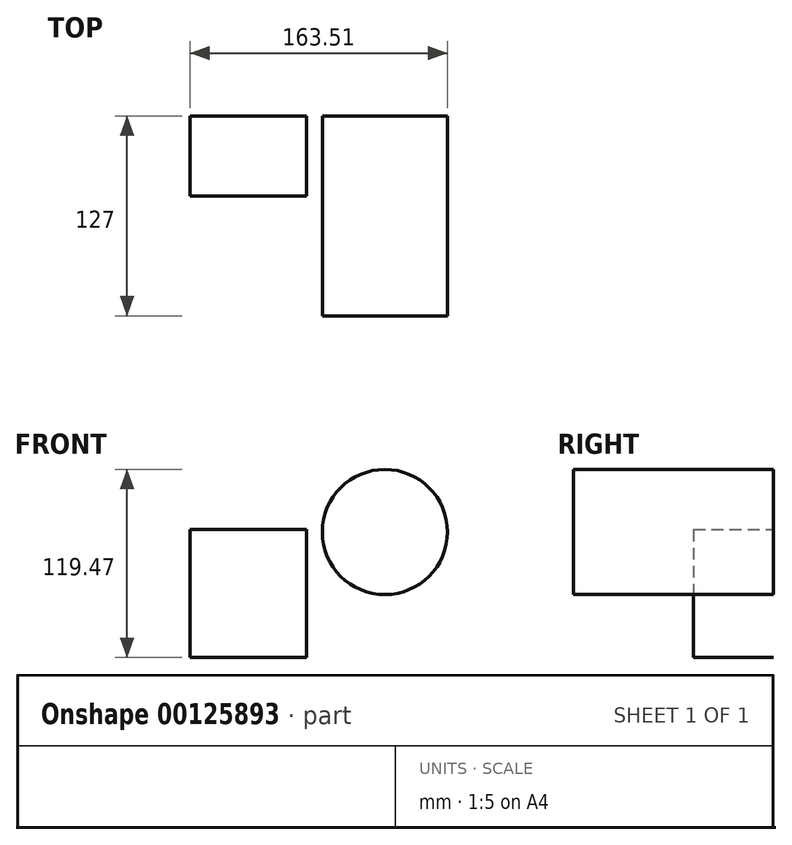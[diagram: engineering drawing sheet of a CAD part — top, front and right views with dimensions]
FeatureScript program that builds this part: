
annotation { "Feature Type Name" : "Feature", "Feature Type Description" : "" }
export const myFeature = defineFeature(function(context is Context, id is Id, definition is map)
    precondition{}
    {
        {
            var Q0;
            Q0=qCreatedBy(makeId("Front.planeOp"),FACE);
            var sketch = newSketch(context, id + "F0", { "sketchPlane" : qUnion([Q0])});
            skLineSegment(sketch, "E0.bottom", {"start": v(-60.74, 34.45) * mm, "end": v(13.29, 34.45) * mm});
            skLineSegment(sketch, "E0.top", {"start": v(-60.74, -46.8) * mm, "end": v(13.29, -46.8) * mm});
            skLineSegment(sketch, "E0.left", {"start": v(-60.74, 34.45) * mm, "end": v(-60.74, -46.8) * mm});
            skLineSegment(sketch, "E0.right", {"start": v(13.29, 34.45) * mm, "end": v(13.29, -46.8) * mm});
            skSolve(sketch);
        }
        {
            var Q0;
            Q0 = qSketchRegion(id + "F0", true);
            extrude(context, id + "F1", {"entities" : qUnion([Q0]), "depth" : 50.8 * mm});
        }
        {
            var Q0;
            Q0=qCreatedBy(makeId("Front.planeOp"),FACE);
            var sketch = newSketch(context, id + "F2", { "sketchPlane" : qUnion([Q0])});
            skCircle(sketch, "E1", {"center": v(63.02, 32.93) * mm, "radius": 39.75 * mm});
            skSolve(sketch);
        }
        {
            var Q0;
            Q0 = qSketchRegion(id + "F2", true);
            extrude(context, id + "F3", {"entities" : qUnion([Q0]), "depth" : 127 * mm});
        }
    });
